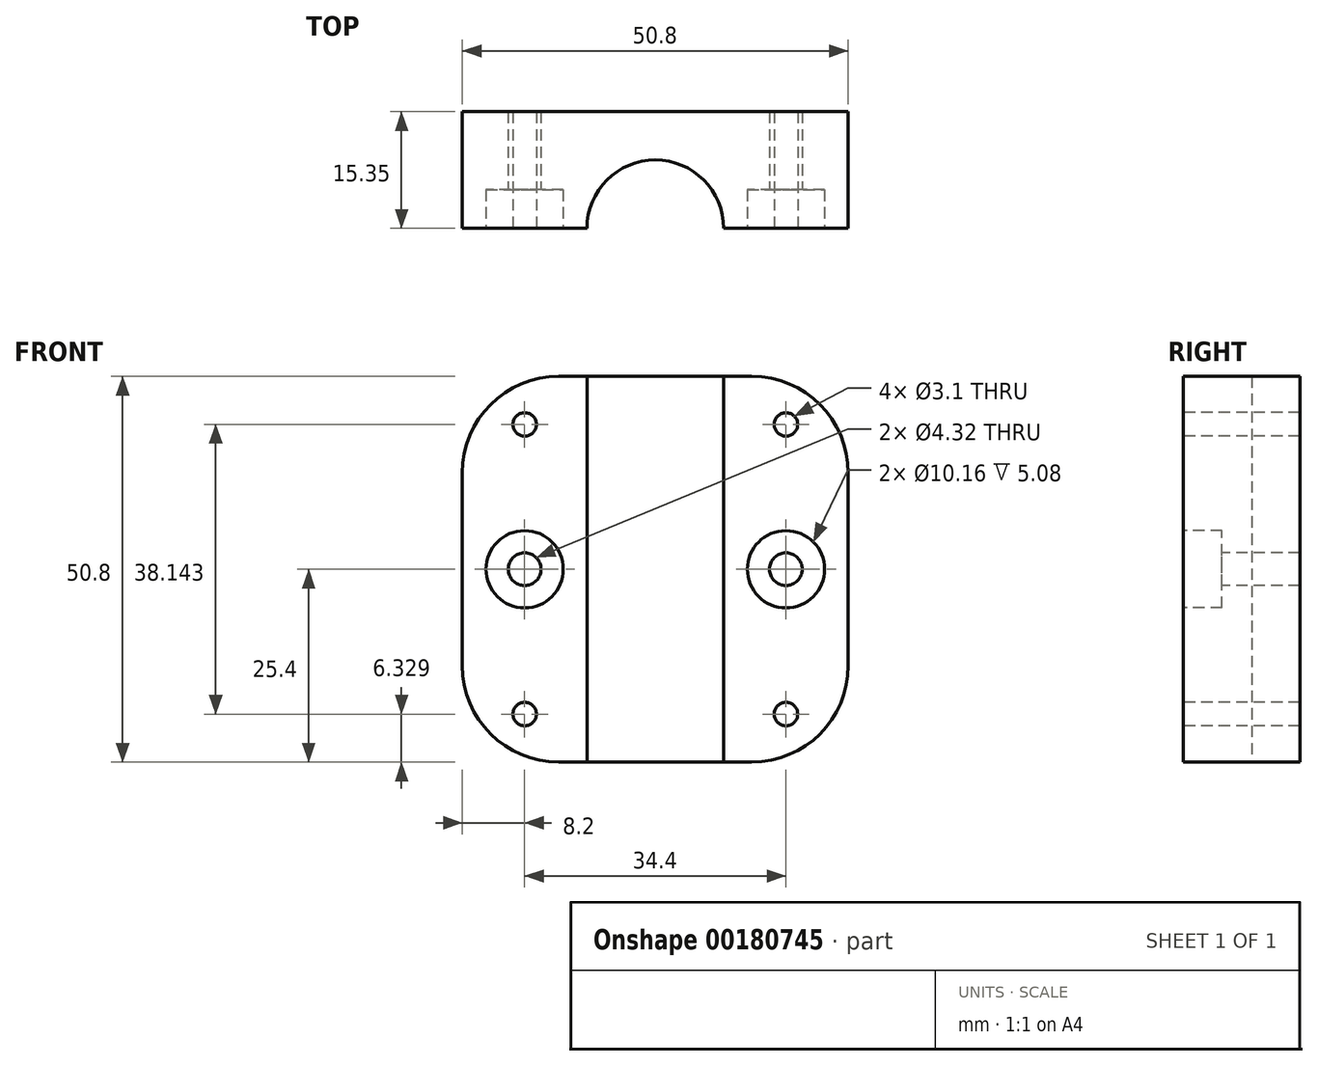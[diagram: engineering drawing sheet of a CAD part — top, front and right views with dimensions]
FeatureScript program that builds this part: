
annotation { "Feature Type Name" : "Feature", "Feature Type Description" : "" }
export const myFeature = defineFeature(function(context is Context, id is Id, definition is map)
    precondition{}
    {
        {
            var Q0;
            Q0=qCreatedBy(makeId("Top.planeOp"),FACE);
            var sketch = newSketch(context, id + "F0", { "sketchPlane" : qUnion([Q0])});
            skLineSegment(sketch, "E0.bottom", {"start": v(25.4, -25.4) * mm, "end": v(-25.4, -25.4) * mm});
            skLineSegment(sketch, "E0.top", {"start": v(25.4, 25.4) * mm, "end": v(-25.4, 25.4) * mm});
            skLineSegment(sketch, "E0.left", {"start": v(25.4, -25.4) * mm, "end": v(25.4, 25.4) * mm});
            skLineSegment(sketch, "E0.right", {"start": v(-25.4, -25.4) * mm, "end": v(-25.4, 25.4) * mm});
            skPoint(sketch, "E0.middle", {"position": v(0, 0) * mm});
            skSolve(sketch);
        }
        {
            var Q0;
            Q0=makeQuery(id+"F0.imprint","IMPRINT",FACE,{"disambiguationData":[TD([[makeQuery(id+"F0.imprint","IMPRINT",EDGE,{"derivedFrom":sQuery(id+"F0.wireOp",EDGE,"E0.bottom")}),-1.0]])]});
            extrude(context, id + "F1", {"entities" : qUnion([Q0]), "depth" : 50.8 * mm});
        }
        {
            var Q0;
            Q0=makeQuery(id+"F1.opExtrude","CAP_FACE",FACE,{"disambiguationData":[OSD([sQuery(id+"F0.wireOp",EDGE,"E0.bottom"),sQuery(id+"F0.wireOp",EDGE,"E0.top"),sQuery(id+"F0.wireOp",EDGE,"E0.left"),sQuery(id+"F0.wireOp",EDGE,"E0.right")])],"isStart":true});
            var sketch = newSketch(context, id + "F2", { "sketchPlane" : qUnion([Q0])});
            skCircle(sketch, "E1", {"center": v(0, 0) * mm, "radius": 9 * mm});
            skSolve(sketch);
        }
        {
            var Q0;
            Q0=qSketchRegion(id+"F2",true);
            extrude(context, id + "F3", {"entities" : qUnion([Q0]), "operationType" : NewBodyOperationType.REMOVE, "oppositeDirection" : true, "depth" : 407.42 * mm});
        }
        {
            var Q0;
            Q0=makeQuery(id+"F1.opExtrude","CAP_FACE",FACE,{"disambiguationData":[OSD([sQuery(id+"F0.wireOp",EDGE,"E0.bottom"),sQuery(id+"F0.wireOp",EDGE,"E0.top"),sQuery(id+"F0.wireOp",EDGE,"E0.left"),sQuery(id+"F0.wireOp",EDGE,"E0.right")])],"isStart":true});
            var sketch = newSketch(context, id + "F4", { "sketchPlane" : qUnion([Q0])});
            skLineSegment(sketch, "E2.bottom", {"start": v(-25.4, 25.4) * mm, "end": v(34.72, 25.4) * mm});
            skLineSegment(sketch, "E2.top", {"start": v(-25.4, 0) * mm, "end": v(34.72, 0) * mm});
            skLineSegment(sketch, "E2.left", {"start": v(-25.4, 25.4) * mm, "end": v(-25.4, 0) * mm});
            skLineSegment(sketch, "E2.right", {"start": v(34.72, 25.4) * mm, "end": v(34.72, 0) * mm});
            skSolve(sketch);
        }
        {
            var Q0;
            Q0=qSketchRegion(id+"F4",true);
            extrude(context, id + "F5", {"entities" : qUnion([Q0]), "operationType" : NewBodyOperationType.REMOVE, "oppositeDirection" : true, "depth" : 338.58 * mm});
        }
        {
            var Q0;
            {var subQ0=sQuery(id+"F0.wireOp",EDGE,"E0.right");Q0=makeQuery(id+"F5.boolean.opBoolean","COPY",FACE,{"disambiguationData":[TD([makeQuery(id+"F1.opExtrude","SWEPT_FACE",FACE,{"disambiguationData":[OSD([subQ0])]})])],"derivedFrom":makeQuery(id+"F5.opExtrude","SWEPT_FACE",FACE,{"disambiguationData":[OSD([sQuery(id+"F4.wireOp",EDGE,"E2.top")])]})});}
            var sketch = newSketch(context, id + "F6", { "sketchPlane" : qUnion([Q0])});
            skCircle(sketch, "E3", {"center": v(-17.2, 25.4) * mm, "radius": 5.08 * mm});
            skSolve(sketch);
        }
        {
            var Q0;
            Q0=qSketchRegion(id+"F6",true);
            extrude(context, id + "F7", {"entities" : qUnion([Q0]), "operationType" : NewBodyOperationType.REMOVE, "oppositeDirection" : true, "depth" : 5.08 * mm});
        }
        {
            var Q0;
            Q0=makeQuery(id+"F7.boolean.opBoolean","COPY",FACE,{"derivedFrom":makeQuery(id+"F7.opExtrude","CAP_FACE",FACE,{"disambiguationData":[OSD([sQuery(id+"F6.wireOp",EDGE,"E3")])],"isStart":false})});
            var sketch = newSketch(context, id + "F8", { "sketchPlane" : qUnion([Q0])});
            skCircle(sketch, "E4", {"center": v(-17.2, 25.4) * mm, "radius": 2.16 * mm});
            skSolve(sketch);
        }
        {
            var Q0;
            Q0=qSketchRegion(id+"F8",true);
            extrude(context, id + "F9", {"entities" : qUnion([Q0]), "operationType" : NewBodyOperationType.REMOVE, "oppositeDirection" : true, "depth" : 25.4 * mm});
        }
        {
            var Q0;
            {var subQ0=sQuery(id+"F0.wireOp",EDGE,"E0.right");Q0=makeQuery(id+"F5.boolean.opBoolean","COPY",FACE,{"disambiguationData":[TD([makeQuery(id+"F1.opExtrude","SWEPT_FACE",FACE,{"disambiguationData":[OSD([subQ0])]})])],"derivedFrom":makeQuery(id+"F5.opExtrude","SWEPT_FACE",FACE,{"disambiguationData":[OSD([sQuery(id+"F4.wireOp",EDGE,"E2.top")])]})});}
            var sketch = newSketch(context, id + "F10", { "sketchPlane" : qUnion([Q0])});
            skCircle(sketch, "E5", {"center": v(-17.2, 44.47) * mm, "radius": 1.55 * mm});
            skPoint(sketch, "E5.centerSnap0", {"position": v(-17.2, 50.8) * mm});
            skSolve(sketch);
        }
        {
            var Q0;
            Q0=qSketchRegion(id+"F10",true);
            extrude(context, id + "F11", {"entities" : qUnion([Q0]), "operationType" : NewBodyOperationType.REMOVE, "oppositeDirection" : true, "depth" : 25.4 * mm});
        }
        {
            var Q0;
            {var subQ0=sQuery(id+"F0.wireOp",EDGE,"E0.right");Q0=makeQuery(id+"F5.boolean.opBoolean","COPY",FACE,{"disambiguationData":[TD([makeQuery(id+"F1.opExtrude","SWEPT_FACE",FACE,{"disambiguationData":[OSD([subQ0])]})])],"derivedFrom":makeQuery(id+"F5.opExtrude","SWEPT_FACE",FACE,{"disambiguationData":[OSD([sQuery(id+"F4.wireOp",EDGE,"E2.top")])]})});}
            var sketch = newSketch(context, id + "F12", { "sketchPlane" : qUnion([Q0])});
            skCircle(sketch, "E6.MirrorC", {"center": v(17.2, 44.47) * mm, "radius": 1.55 * mm});
            skCircle(sketch, "E7.MirrorC", {"center": v(17.2, 25.4) * mm, "radius": 5.08 * mm, "construction": true});
            skCircle(sketch, "E8.MirrorC", {"center": v(17.2, 25.4) * mm, "radius": 2.16 * mm});
            skSolve(sketch);
        }
        {
            var Q0;
            Q0=qSketchRegion(id+"F12",true);
            extrude(context, id + "F13", {"entities" : qUnion([Q0]), "operationType" : NewBodyOperationType.REMOVE, "oppositeDirection" : true, "depth" : 25.4 * mm});
        }
        {
            var Q0;
            {var subQ1=sQuery(id+"F0.wireOp",EDGE,"E0.left");Q0=makeQuery(id+"F5.boolean.opBoolean","COPY",FACE,{"disambiguationData":[TD([makeQuery(id+"F1.opExtrude","SWEPT_FACE",FACE,{"disambiguationData":[OSD([subQ1])]})])],"derivedFrom":makeQuery(id+"F5.opExtrude","SWEPT_FACE",FACE,{"disambiguationData":[OSD([sQuery(id+"F4.wireOp",EDGE,"E2.top")])]})});}
            var sketch = newSketch(context, id + "F14", { "sketchPlane" : qUnion([Q0])});
            skCircle(sketch, "E9.MirrorC", {"center": v(17.2, 25.4) * mm, "radius": 5.08 * mm});
            skSolve(sketch);
        }
        {
            var Q0;
            Q0=qSketchRegion(id+"F14",true);
            extrude(context, id + "F15", {"entities" : qUnion([Q0]), "operationType" : NewBodyOperationType.REMOVE, "oppositeDirection" : true, "depth" : 5.08 * mm});
        }
        {
            var Q0;
            Q0=makeQuery(id+"F1.opExtrude","CAP_FACE",FACE,{"disambiguationData":[OSD([sQuery(id+"F0.wireOp",EDGE,"E0.bottom"),sQuery(id+"F0.wireOp",EDGE,"E0.top"),sQuery(id+"F0.wireOp",EDGE,"E0.left"),sQuery(id+"F0.wireOp",EDGE,"E0.right")])],"isStart":false});
            cPlane(context, id + "F16", {"entities" : qUnion([Q0]), "cplaneType" : CPlaneType.OFFSET, "offset" : 25.4 * mm, "oppositeDirection" : true, "width" : 152.4 * mm, "height" : 152.4 * mm});
        }
        {
            var Q0;
            Q0=makeQuery(id+"F1.opExtrude","SWEPT_BODY",BODY,{"disambiguationData":[OSD([sQuery(id+"F0.wireOp",EDGE,"E0.bottom"),sQuery(id+"F0.wireOp",EDGE,"E0.top"),sQuery(id+"F0.wireOp",EDGE,"E0.left"),sQuery(id+"F0.wireOp",EDGE,"E0.right")])]});
            var Q1;
            Q1=qCreatedBy(id+"F16.planeOp",FACE);
            mirror(context, id + "F17", {"operationType" : NewBodyOperationType.INTERSECT, "entities" : qUnion([Q0]), "mirrorPlane" : qUnion([Q1])});
        }
        {
            var Q0;
            Q0=makeQuery(id+"F1.opExtrude","CAP_FACE",FACE,{"disambiguationData":[OSD([sQuery(id+"F0.wireOp",EDGE,"E0.bottom"),sQuery(id+"F0.wireOp",EDGE,"E0.top"),sQuery(id+"F0.wireOp",EDGE,"E0.left"),sQuery(id+"F0.wireOp",EDGE,"E0.right")])],"isStart":true});
            var sketch = newSketch(context, id + "F18", { "sketchPlane" : qUnion([Q0])});
            skLineSegment(sketch, "E10", {"start": v(0, -9) * mm, "end": v(0, -15.35) * mm});
            skLineSegment(sketch, "E11", {"start": v(0, -15.35) * mm, "end": v(-44.71, -15.35) * mm});
            skLineSegment(sketch, "E12", {"start": v(-44.71, -15.35) * mm, "end": v(-42.65, -31.93) * mm});
            skLineSegment(sketch, "E13", {"start": v(-42.65, -31.93) * mm, "end": v(43.38, -33.96) * mm});
            skLineSegment(sketch, "E14", {"start": v(0, -15.35) * mm, "end": v(37.31, -15.35) * mm});
            skLineSegment(sketch, "E15", {"start": v(37.31, -15.35) * mm, "end": v(43.38, -33.96) * mm});
            skSolve(sketch);
        }
        {
            var Q0;
            Q0=qSketchRegion(id+"F18",true);
            extrude(context, id + "F19", {"entities" : qUnion([Q0]), "operationType" : NewBodyOperationType.REMOVE, "oppositeDirection" : true, "depth" : 72.39 * mm});
        }
        {
            var Q0;
            {var subQ0=sQuery(id+"F0.wireOp",EDGE,"E0.right");Q0=makeQuery(id+"F5.boolean.opBoolean","COPY",FACE,{"disambiguationData":[TD([makeQuery(id+"F1.opExtrude","SWEPT_FACE",FACE,{"disambiguationData":[OSD([subQ0])]})])],"derivedFrom":makeQuery(id+"F5.opExtrude","SWEPT_FACE",FACE,{"disambiguationData":[OSD([sQuery(id+"F4.wireOp",EDGE,"E2.top")])]})});}
            var sketch = newSketch(context, id + "F20", { "sketchPlane" : qUnion([Q0])});
            skLineSegment(sketch, "E16.bottom", {"start": v(-21.86, 2.54) * mm, "end": v(-9.9, 2.54) * mm});
            skLineSegment(sketch, "E16.top", {"start": v(-21.86, 48.26) * mm, "end": v(-9.9, 48.26) * mm});
            skLineSegment(sketch, "E16.left", {"start": v(-21.86, 2.54) * mm, "end": v(-21.86, 48.26) * mm});
            skLineSegment(sketch, "E16.right", {"start": v(21.86, 2.54) * mm, "end": v(21.86, 48.26) * mm});
            skPoint(sketch, "E16.middle", {"position": v(0, 25.4) * mm});
            skPoint(sketch, "E16.middle.positionSnap0", {"position": v(-25.4, 25.4) * mm});
            skPoint(sketch, "E16.centerSnap0", {"position": v(-25.4, 25.4) * mm});
            skLineSegment(sketch, "E17.0", {"start": v(-9.9, 48.26) * mm, "end": v(-9.9, 2.54) * mm});
            skLineSegment(sketch, "E18", {"start": v(9.9, 48.26) * mm, "end": v(9.9, 2.54) * mm});
            skLineSegment(sketch, "E19.trimOffspring", {"start": v(9.9, 48.26) * mm, "end": v(21.86, 48.26) * mm});
            skPoint(sketch, "E20.orphan", {"position": v(0, 2.54) * mm});
            skPoint(sketch, "E21.start.orphan", {"position": v(0, 48.26) * mm});
            skLineSegment(sketch, "E22.trimOffspring", {"start": v(9.9, 2.54) * mm, "end": v(21.86, 2.54) * mm});
            skSolve(sketch);
        }
        {
            var Q0;
            {var subQ1=sQuery(id+"F0.wireOp",EDGE,"E0.left");Q0=makeQuery(id+"F5.boolean.opBoolean","COPY",FACE,{"disambiguationData":[TD([makeQuery(id+"F1.opExtrude","SWEPT_FACE",FACE,{"disambiguationData":[OSD([subQ1])]})])],"derivedFrom":makeQuery(id+"F5.opExtrude","SWEPT_FACE",FACE,{"disambiguationData":[OSD([sQuery(id+"F4.wireOp",EDGE,"E2.top")])]})});}
            var sketch = newSketch(context, id + "F21", { "sketchPlane" : qUnion([Q0])});
            skCircle(sketch, "E23.0", {"center": v(-17.2, 44.47) * mm, "radius": 1.55 * mm});
            skCircle(sketch, "E24.0", {"center": v(-17.2, 25.4) * mm, "radius": 5.08 * mm});
            skArc(sketch, "E25", {"start": v(-18.8, 33.22) * mm, "mid": v(-17.18, 17.42) * mm, "end": v(-15.62, 33.23) * mm});
            skLineSegment(sketch, "E26.0", {"start": v(-18.8, 41.9) * mm, "end": v(-18.8, 33.22) * mm});
            skArc(sketch, "E27", {"start": v(-15.62, 41.89) * mm, "mid": v(-17.18, 47.5) * mm, "end": v(-18.8, 41.9) * mm});
            skLineSegment(sketch, "E28.0", {"start": v(-15.62, 41.89) * mm, "end": v(-15.62, 33.23) * mm});
            skLineSegment(sketch, "E29.0", {"start": v(-9, 47.6) * mm, "end": v(-22.2, 47.6) * mm});
            skLineSegment(sketch, "E29.1", {"start": v(-9, 47.6) * mm, "end": v(9, 47.6) * mm});
            skLineSegment(sketch, "E29.2", {"start": v(-22.2, 47.6) * mm, "end": v(-22.2, 3.2) * mm});
            skLineSegment(sketch, "E29.3", {"start": v(22.2, 47.6) * mm, "end": v(9, 47.6) * mm});
            skLineSegment(sketch, "E29.4", {"start": v(-22.2, 3.2) * mm, "end": v(-9, 3.2) * mm});
            skLineSegment(sketch, "E29.5", {"start": v(9, 3.2) * mm, "end": v(-9, 3.2) * mm});
            skLineSegment(sketch, "E29.6", {"start": v(9, 3.2) * mm, "end": v(22.2, 3.2) * mm});
            skLineSegment(sketch, "E29.7", {"start": v(22.2, 47.6) * mm, "end": v(22.2, 3.2) * mm});
            skLineSegment(sketch, "E30", {"start": v(-12.18, 47.6) * mm, "end": v(-12.18, 3.2) * mm});
            skLineSegment(sketch, "E31.0", {"start": v(-9, 50.8) * mm, "end": v(-9, 0) * mm, "construction": true});
            skSolve(sketch);
        }
        {
            var Q0;
            Q0=makeQuery(id+"F1.opExtrude","CAP_EDGE",EDGE,{"disambiguationData":[OSD([sQuery(id+"F0.wireOp",EDGE,"E0.left")])],"isStart":false});
            var Q1;
            Q1=makeQuery(id+"F1.opExtrude","CAP_EDGE",EDGE,{"disambiguationData":[OSD([sQuery(id+"F0.wireOp",EDGE,"E0.left")])],"isStart":true});
            var Q2;
            Q2=makeQuery(id+"F1.opExtrude","CAP_EDGE",EDGE,{"disambiguationData":[OSD([sQuery(id+"F0.wireOp",EDGE,"E0.right")])],"isStart":false});
            var Q3;
            Q3=makeQuery(id+"F1.opExtrude","CAP_EDGE",EDGE,{"disambiguationData":[OSD([sQuery(id+"F0.wireOp",EDGE,"E0.right")])],"isStart":true});
            fillet(context, id + "F22", {"entities" : qUnion([Q0, Q1, Q2, Q3]), "radius" : 12.7 * mm, "tangentPropagation" : true, "allowEdgeOverflow" : false});
        }
    });
